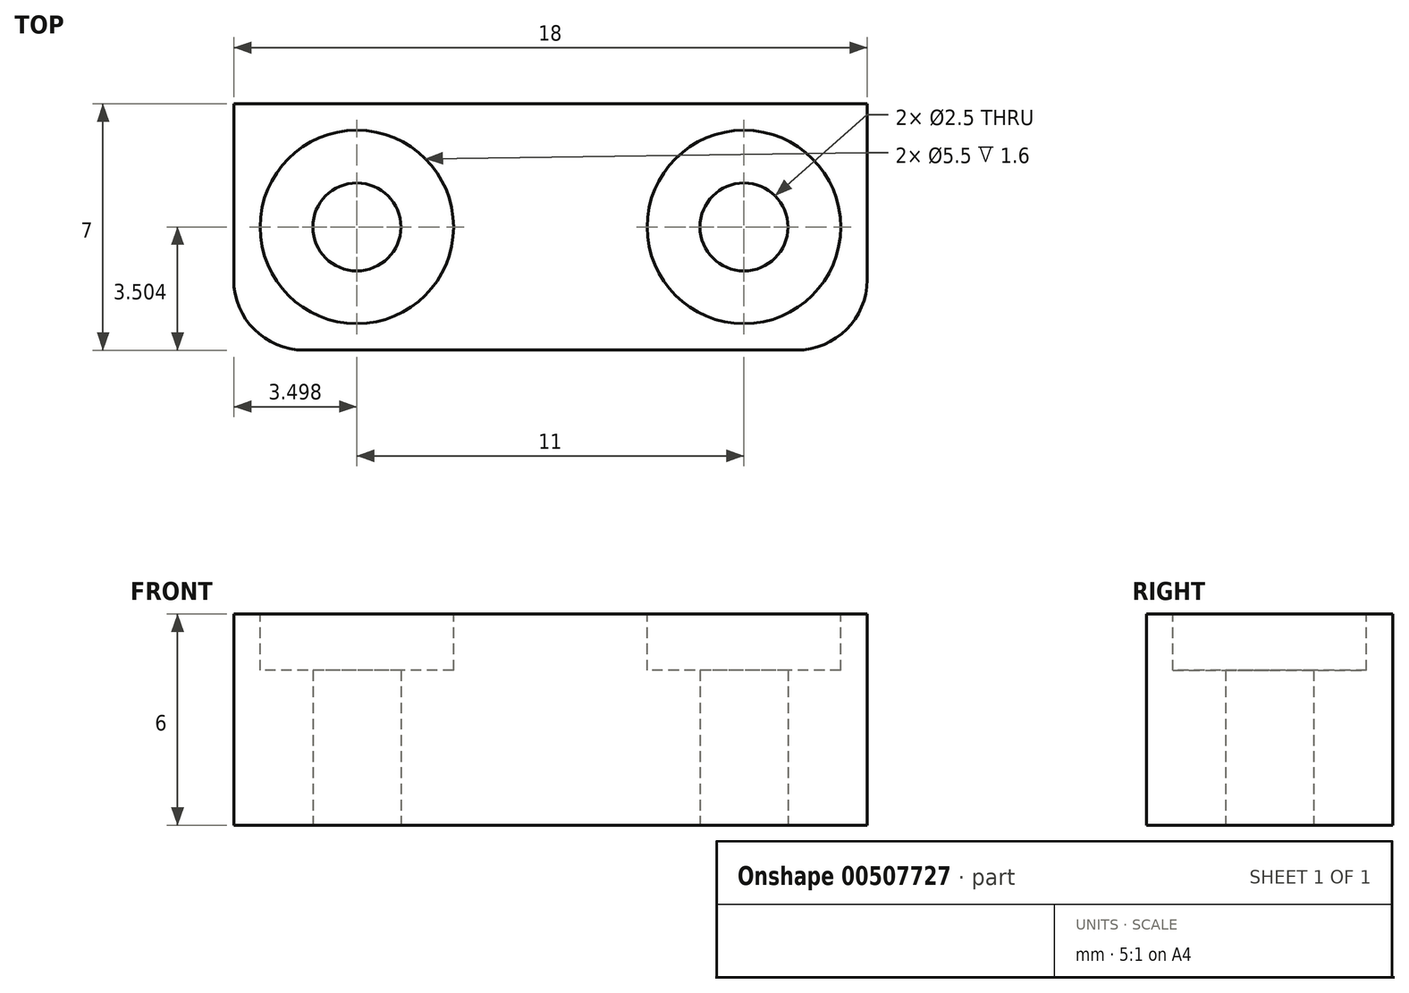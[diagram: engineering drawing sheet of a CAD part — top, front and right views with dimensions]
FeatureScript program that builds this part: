
annotation { "Feature Type Name" : "Feature", "Feature Type Description" : "" }
export const myFeature = defineFeature(function(context is Context, id is Id, definition is map)
    precondition{}
    {
        {
            var Q0;
            Q0=qCreatedBy(makeId("Top.planeOp"),FACE);
            var sketch = newSketch(context, id + "F0", { "sketchPlane" : qUnion([Q0])});
            skLineSegment(sketch, "E0.bottom", {"start": v(40.49, 56.33) * mm, "end": v(58.49, 56.33) * mm});
            skLineSegment(sketch, "E0.top", {"start": v(42.49, 49.33) * mm, "end": v(56.49, 49.33) * mm});
            skLineSegment(sketch, "E0.left", {"start": v(40.49, 56.33) * mm, "end": v(40.49, 51.33) * mm});
            skLineSegment(sketch, "E0.right", {"start": v(58.49, 56.33) * mm, "end": v(58.49, 51.33) * mm});
            skPoint(sketch, "E1.visualSharp", {"position": v(58.49, 49.33) * mm});
            skArc(sketch, "E1.filletArc", {"start": v(56.49, 49.33) * mm, "mid": v(57.9, 49.92) * mm, "end": v(58.49, 51.33) * mm});
            skPoint(sketch, "E2.visualSharp", {"position": v(40.49, 49.33) * mm});
            skArc(sketch, "E2.filletArc", {"start": v(40.49, 51.33) * mm, "mid": v(41.07, 49.92) * mm, "end": v(42.49, 49.33) * mm});
            skCircle(sketch, "E3", {"center": v(54.99, 52.83) * mm, "radius": 1.25 * mm});
            skCircle(sketch, "E4", {"center": v(43.99, 52.83) * mm, "radius": 1.25 * mm});
            skSolve(sketch);
        }
        {
            var Q0;
            Q0=qSketchRegion(id+"F0",true);
            extrude(context, id + "F1", {"entities" : qUnion([Q0]), "depth" : 6 * mm, "offsetDistance" : 25 * mm});
        }
        {
            var Q0;
            Q0=makeQuery(id+"F1.opExtrude","CAP_FACE",FACE,{"disambiguationData":[OSD([sQuery(id+"F0.wireOp",EDGE,"E0.bottom"),sQuery(id+"F0.wireOp",EDGE,"E0.top"),sQuery(id+"F0.wireOp",EDGE,"E0.left"),sQuery(id+"F0.wireOp",EDGE,"E0.right"),sQuery(id+"F0.wireOp",EDGE,"E1.filletArc"),sQuery(id+"F0.wireOp",EDGE,"E2.filletArc"),sQuery(id+"F0.wireOp",EDGE,"E3"),sQuery(id+"F0.wireOp",EDGE,"E4")])],"isStart":false});
            var sketch = newSketch(context, id + "F2", { "sketchPlane" : qUnion([Q0])});
            skCircle(sketch, "E5.0", {"center": v(54.99, 52.83) * mm, "radius": 2.75 * mm});
            skCircle(sketch, "E6.0", {"center": v(43.99, 52.83) * mm, "radius": 2.75 * mm});
            skSolve(sketch);
        }
        {
            var Q0;
            Q0=qSketchRegion(id+"F2",true);
            extrude(context, id + "F3", {"entities" : qUnion([Q0]), "operationType" : NewBodyOperationType.REMOVE, "oppositeDirection" : true, "depth" : 1.6 * mm, "offsetDistance" : 25 * mm});
        }
    });
